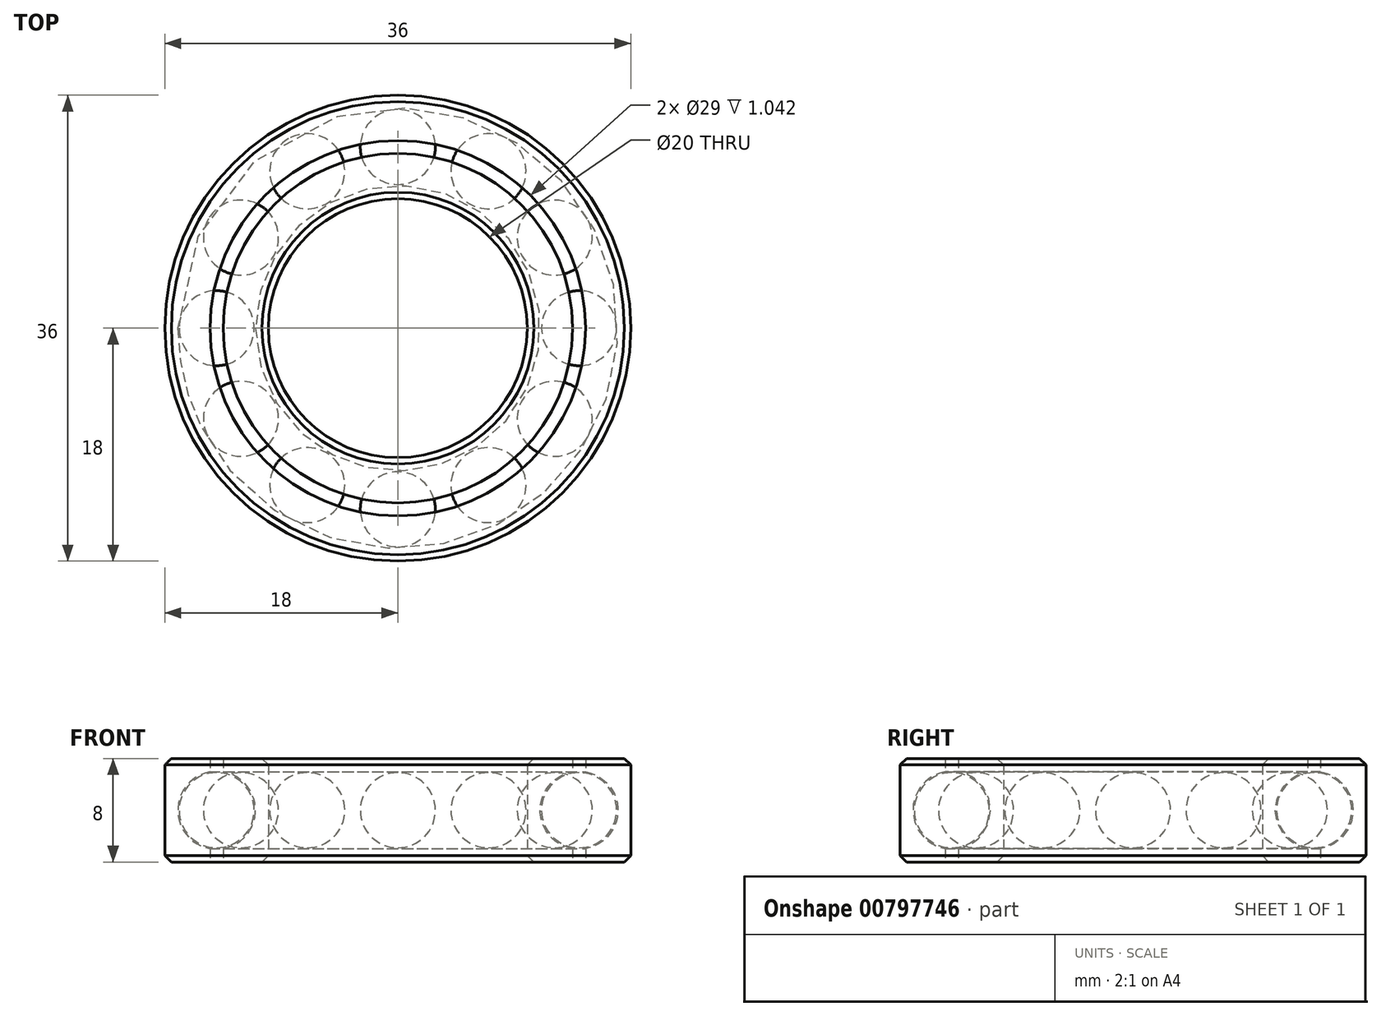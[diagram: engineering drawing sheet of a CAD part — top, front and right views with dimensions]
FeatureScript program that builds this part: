
annotation { "Feature Type Name" : "Feature", "Feature Type Description" : "" }
export const myFeature = defineFeature(function(context is Context, id is Id, definition is map)
    precondition{}
    {
        {
            assignVariable(context, id + "F0", {"name" : "espacio_alto", "anyValue" : 156});
        }
        {
            assignVariable(context, id + "F1", {"name" : "espacio_atras", "anyValue" : 0});
        }
        {
            assignVariable(context, id + "F2", {"name" : "espacio_lateral", "anyValue" : 0});
        }
        {
            var Q0;
            Q0=qCreatedBy(makeId("Right.planeOp"),FACE);
            var sketch = newSketch(context, id + "F3", { "sketchPlane" : qUnion([Q0])});
            skLineSegment(sketch, "E0", {"start": v(0, 0) * mm, "end": v(0, 7.32) * mm, "construction": true});
            skArc(sketch, "E1", {"start": v(14, 3) * mm, "mid": v(17, 0) * mm, "end": v(14, -3) * mm});
            skLineSegment(sketch, "E2", {"start": v(14, 3) * mm, "end": v(14, -3) * mm});
            skLineSegment(sketch, "E3", {"start": v(14.5, 2.96) * mm, "end": v(14.5, -2.96) * mm});
            skLineSegment(sketch, "E4", {"start": v(14, 3) * mm, "end": v(14, 4) * mm});
            skLineSegment(sketch, "E5", {"start": v(14, 4) * mm, "end": v(18, 4) * mm});
            skLineSegment(sketch, "E6", {"start": v(18, 4) * mm, "end": v(18, 0) * mm});
            skLineSegment(sketch, "E7", {"start": v(0, 0) * mm, "end": v(-2.34, 0) * mm, "construction": true});
            skLineSegment(sketch, "E8.MirrorCS", {"start": v(14, -4) * mm, "end": v(18, -4) * mm});
            skLineSegment(sketch, "E9.MirrorCS", {"start": v(18, -4) * mm, "end": v(18, 0) * mm});
            skLineSegment(sketch, "E10.MirrorCS", {"start": v(14, -3) * mm, "end": v(14, -4) * mm});
            skLineSegment(sketch, "E11.MirrorCS", {"start": v(14, 4) * mm, "end": v(10, 4) * mm});
            skLineSegment(sketch, "E12.MirrorCS", {"start": v(10, 4) * mm, "end": v(10, 0) * mm});
            skLineSegment(sketch, "E13.MirrorCS", {"start": v(13.5, 2.96) * mm, "end": v(13.5, -2.96) * mm});
            skArc(sketch, "E14.MirrorCS", {"start": v(14, 3) * mm, "mid": v(11, 0) * mm, "end": v(14, -3) * mm});
            skLineSegment(sketch, "E15.MirrorCS", {"start": v(14, -4) * mm, "end": v(10, -4) * mm});
            skLineSegment(sketch, "E16.MirrorCS", {"start": v(10, -4) * mm, "end": v(10, 0) * mm});
            skLineSegment(sketch, "E17", {"start": v(13.5, -4) * mm, "end": v(13.5, 4) * mm});
            skLineSegment(sketch, "E18", {"start": v(14.5, -4) * mm, "end": v(14.5, 4) * mm});
            skSolve(sketch);
        }
        {
            var Q0;
            Q0=qCreatedBy(makeId("Right.planeOp"),FACE);
            var sketch = newSketch(context, id + "F4", { "sketchPlane" : qUnion([Q0])});
            skArc(sketch, "E19.0", {"start": v(14, 2.9) * mm, "mid": v(11.1, 0) * mm, "end": v(14, -2.9) * mm});
            skLineSegment(sketch, "E20", {"start": v(14, 2.9) * mm, "end": v(14, -2.9) * mm});
            skSolve(sketch);
        }
        {
            var Q0;
            Q0=makeQuery(id+"F4.imprint","IMPRINT",FACE,{"disambiguationData":[TD([[makeQuery(id+"F4.imprint","IMPRINT",EDGE,{"derivedFrom":sQuery(id+"F4.wireOp",EDGE,"E19.0")}),1.0]])]});
            var Q1;
            Q1=sQuery(id+"F4.wireOp",EDGE,"E20");
            revolve(context, id + "F5", {"surfaceOperationType" : NewSurfaceOperationType.NEW, "entities" : qUnion([Q0]), "axis" : qUnion([Q1]), "revolveType" : RevolveType.FULL});
        }
        {
            var Q0;
            {var subQ7=sQuery(id+"F3.wireOp",EDGE,"E12.MirrorCS");Q0=makeQuery(id+"F3.imprint","IMPRINT",FACE,{"disambiguationData":[TD([[makeQuery(id+"F3.imprint","IMPRINT",EDGE,{"derivedFrom":subQ7}),1.0]])]});}
            var Q1;
            {var subQ4=sQuery(id+"F3.wireOp",EDGE,"E6");Q1=makeQuery(id+"F3.imprint","IMPRINT",FACE,{"disambiguationData":[TD([[makeQuery(id+"F3.imprint","IMPRINT",EDGE,{"derivedFrom":subQ4}),-1.0]])]});}
            var Q2;
            Q2=sQuery(id+"F3.wireOp",EDGE,"E0");
            revolve(context, id + "F6", {"surfaceOperationType" : NewSurfaceOperationType.NEW, "entities" : qUnion([Q0, Q1]), "axis" : qUnion([Q2]), "revolveType" : RevolveType.FULL});
        }
        {
            var Q0;
            Q0=makeQuery(id+"F6.opRevolve","SWEPT_EDGE",EDGE,{"disambiguationData":[OSD([sQuery(id+"F3.wireOp",EDGE,"E5"),sQuery(id+"F3.wireOp",EDGE,"E6")])]});
            var Q1;
            Q1=makeQuery(id+"F6.opRevolve","SWEPT_EDGE",EDGE,{"disambiguationData":[OSD([sQuery(id+"F3.wireOp",EDGE,"E8.MirrorCS"),sQuery(id+"F3.wireOp",EDGE,"E9.MirrorCS")])]});
            var Q2;
            Q2=makeQuery(id+"F6.opRevolve","SWEPT_EDGE",EDGE,{"disambiguationData":[OSD([sQuery(id+"F3.wireOp",EDGE,"E11.MirrorCS"),sQuery(id+"F3.wireOp",EDGE,"E12.MirrorCS")])]});
            var Q3;
            Q3=makeQuery(id+"F6.opRevolve","SWEPT_EDGE",EDGE,{"disambiguationData":[OSD([sQuery(id+"F3.wireOp",EDGE,"E15.MirrorCS"),sQuery(id+"F3.wireOp",EDGE,"E16.MirrorCS")])]});
            chamfer(context, id + "F7", {"entities" : qUnion([Q0, Q1, Q2, Q3]), "width" : 0.5 * mm, "tangentPropagation" : true});
        }
        {
            var Q0;
            Q0=makeQuery(id+"F5.opRevolve","SWEPT_BODY",BODY,{"disambiguationData":[OSD([sQuery(id+"F4.wireOp",EDGE,"E19.0"),sQuery(id+"F4.wireOp",EDGE,"E20")])]});
            var Q1;
            Q1=sQuery(id+"F3.wireOp",EDGE,"E0");
            circularPattern(context, id + "F8", {"entities" : qUnion([Q0]), "axis" : qUnion([Q1]), "angle" : 360 * degree, "instanceCount" : 12, "equalSpace" : true});
        }
        {
            var Q0;
            Q0=makeQuery(id+"F6.opRevolve","SWEPT_BODY",BODY,{"disambiguationData":[OSD([sQuery(id+"F3.wireOp",EDGE,"E11.MirrorCS"),sQuery(id+"F3.wireOp",EDGE,"E12.MirrorCS"),sQuery(id+"F3.wireOp",EDGE,"E14.MirrorCS"),sQuery(id+"F3.wireOp",EDGE,"E15.MirrorCS"),sQuery(id+"F3.wireOp",EDGE,"E16.MirrorCS"),sQuery(id+"F3.wireOp",EDGE,"E17")])]});
            var Q1;
            Q1=makeQuery(id+"F8.opPattern","COPY",BODY,{"derivedFrom":makeQuery(id+"F5.opRevolve","SWEPT_BODY",BODY,{"disambiguationData":[OSD([sQuery(id+"F4.wireOp",EDGE,"E19.0"),sQuery(id+"F4.wireOp",EDGE,"E20")])]}),"instanceName":"8"});
            var Q2;
            Q2=makeQuery(id+"F6.opRevolve","SWEPT_BODY",BODY,{"disambiguationData":[OSD([sQuery(id+"F3.wireOp",EDGE,"E1"),sQuery(id+"F3.wireOp",EDGE,"E5"),sQuery(id+"F3.wireOp",EDGE,"E6"),sQuery(id+"F3.wireOp",EDGE,"E8.MirrorCS"),sQuery(id+"F3.wireOp",EDGE,"E9.MirrorCS"),sQuery(id+"F3.wireOp",EDGE,"E18")])]});
            var Q3;
            Q3=makeQuery(id+"F8.opPattern","COPY",BODY,{"derivedFrom":makeQuery(id+"F5.opRevolve","SWEPT_BODY",BODY,{"disambiguationData":[OSD([sQuery(id+"F4.wireOp",EDGE,"E19.0"),sQuery(id+"F4.wireOp",EDGE,"E20")])]}),"instanceName":"3"});
            var Q4;
            Q4=makeQuery(id+"F8.opPattern","COPY",BODY,{"derivedFrom":makeQuery(id+"F5.opRevolve","SWEPT_BODY",BODY,{"disambiguationData":[OSD([sQuery(id+"F4.wireOp",EDGE,"E19.0"),sQuery(id+"F4.wireOp",EDGE,"E20")])]}),"instanceName":"5"});
            var Q5;
            Q5=makeQuery(id+"F8.opPattern","COPY",BODY,{"derivedFrom":makeQuery(id+"F5.opRevolve","SWEPT_BODY",BODY,{"disambiguationData":[OSD([sQuery(id+"F4.wireOp",EDGE,"E19.0"),sQuery(id+"F4.wireOp",EDGE,"E20")])]}),"instanceName":"11"});
            var Q6;
            Q6=makeQuery(id+"F8.opPattern","COPY",BODY,{"derivedFrom":makeQuery(id+"F5.opRevolve","SWEPT_BODY",BODY,{"disambiguationData":[OSD([sQuery(id+"F4.wireOp",EDGE,"E19.0"),sQuery(id+"F4.wireOp",EDGE,"E20")])]}),"instanceName":"6"});
            var Q7;
            Q7=makeQuery(id+"F8.opPattern","COPY",BODY,{"derivedFrom":makeQuery(id+"F5.opRevolve","SWEPT_BODY",BODY,{"disambiguationData":[OSD([sQuery(id+"F4.wireOp",EDGE,"E19.0"),sQuery(id+"F4.wireOp",EDGE,"E20")])]}),"instanceName":"9"});
            var Q8;
            Q8=makeQuery(id+"F8.opPattern","COPY",BODY,{"derivedFrom":makeQuery(id+"F5.opRevolve","SWEPT_BODY",BODY,{"disambiguationData":[OSD([sQuery(id+"F4.wireOp",EDGE,"E19.0"),sQuery(id+"F4.wireOp",EDGE,"E20")])]}),"instanceName":"1"});
            var Q9;
            Q9=makeQuery(id+"F8.opPattern","COPY",BODY,{"derivedFrom":makeQuery(id+"F5.opRevolve","SWEPT_BODY",BODY,{"disambiguationData":[OSD([sQuery(id+"F4.wireOp",EDGE,"E19.0"),sQuery(id+"F4.wireOp",EDGE,"E20")])]}),"instanceName":"7"});
            var Q10;
            Q10=makeQuery(id+"F8.opPattern","COPY",BODY,{"derivedFrom":makeQuery(id+"F5.opRevolve","SWEPT_BODY",BODY,{"disambiguationData":[OSD([sQuery(id+"F4.wireOp",EDGE,"E19.0"),sQuery(id+"F4.wireOp",EDGE,"E20")])]}),"instanceName":"2"});
            var Q11;
            Q11=makeQuery(id+"F8.opPattern","COPY",BODY,{"derivedFrom":makeQuery(id+"F5.opRevolve","SWEPT_BODY",BODY,{"disambiguationData":[OSD([sQuery(id+"F4.wireOp",EDGE,"E19.0"),sQuery(id+"F4.wireOp",EDGE,"E20")])]}),"instanceName":"4"});
            var Q12;
            Q12=makeQuery(id+"F8.opPattern","COPY",BODY,{"derivedFrom":makeQuery(id+"F5.opRevolve","SWEPT_BODY",BODY,{"disambiguationData":[OSD([sQuery(id+"F4.wireOp",EDGE,"E19.0"),sQuery(id+"F4.wireOp",EDGE,"E20")])]}),"instanceName":"10"});
            var Q13;
            Q13=makeQuery(id+"F5.opRevolve","SWEPT_BODY",BODY,{"disambiguationData":[OSD([sQuery(id+"F4.wireOp",EDGE,"E19.0"),sQuery(id+"F4.wireOp",EDGE,"E20")])]});
            transform(context, id + "F9", {"entities" : qUnion([Q0, Q1, Q2, Q3, Q4, Q5, Q6, Q7, Q8, Q9, Q10, Q11, Q12, Q13]), "transformType" : TransformType.TRANSLATION_3D, "dx" : (getVariable(context, 'espacio_lateral')) * mm, "dy" : (getVariable(context, 'espacio_atras')) * mm, "dz" : (getVariable(context, 'espacio_alto')) * mm, "makeCopy" : false});
        }
        {
            var Q0;
            Q0=qCreatedBy(makeId("Top.planeOp"),FACE);
            var sketch = newSketch(context, id + "F10", { "sketchPlane" : qUnion([Q0])});
            skLineSegment(sketch, "E21.bottom", {"start": v(53.03, 41.37) * mm, "end": v(125.55, 41.37) * mm});
            skLineSegment(sketch, "E21.top", {"start": v(53.03, 143.66) * mm, "end": v(125.55, 143.66) * mm});
            skLineSegment(sketch, "E21.left", {"start": v(53.03, 41.37) * mm, "end": v(53.03, 143.66) * mm});
            skLineSegment(sketch, "E21.right", {"start": v(125.55, 41.37) * mm, "end": v(125.55, 143.66) * mm});
            skSolve(sketch);
        }
        {
            var Q0;
            Q0 = qSketchRegion(id + "F10", true);
            extrude(context, id + "F11", {"entities" : qUnion([Q0]), "depth" : 25 * mm, "offsetDistance" : 25 * mm});
        }
        {
            var Q0;
            Q0=makeQuery(id+"F11.opExtrude","SWEPT_BODY",BODY,{"disambiguationData":[OSD([sQuery(id+"F10.wireOp",EDGE,"E21.bottom"),sQuery(id+"F10.wireOp",EDGE,"E21.top"),sQuery(id+"F10.wireOp",EDGE,"E21.left"),sQuery(id+"F10.wireOp",EDGE,"E21.right")])]});
            deleteBodies(context, id + "F12", {"entities" : qUnion([Q0])});
        }
    });
